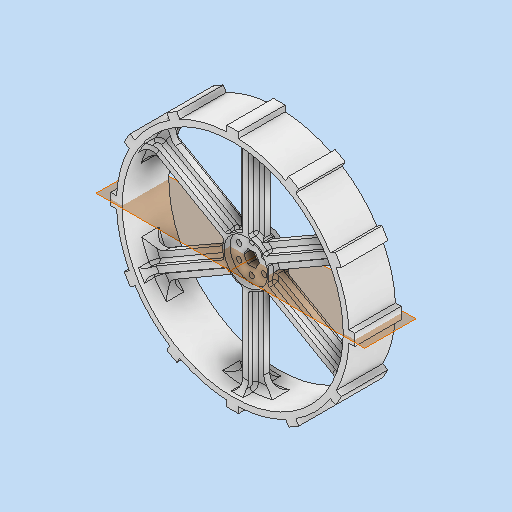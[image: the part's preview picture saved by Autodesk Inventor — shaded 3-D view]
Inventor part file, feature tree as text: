
AUTODESK INVENTOR PART (.ipt)
format: ipt  version: 2023 (Build 270158000, 158)  size: 903,168 bytes
history: native  units: in
note: dims shown in document units (in); Inventor stores cm internally (conversion verified against a paired STEP export)
features: fillet x5, sketch x5, extrude x4, pattern_circular x2
ambient origin geometry x8: Origin, YZ Plane, XZ Plane, XY Plane, X Axis, Y Axis, Z Axis, Center Point
bodies: Solid1 (feature_tree)
feature tree (16):
  extrude  "Extrusion1"  Depth=0.25in
  extrude  "Extrusion2"  Depth=2.0in
  extrude  "Extrusion3"  Depth=0.375in TaperAngle=0.0deg
  extrude  "Extrusion4"  Depth=0.25in
  fillet  "Fillet2"  Radius=0.875in
  fillet  "Fillet3"  Radius=0.25in
  fillet  "Fillet4"  Radius=0.875in
  fillet  "Fillet1"  Radius=0.9375in
  fillet  "Fillet5"  Radius=0.25in
  pattern_circular  "Circular Pattern1"  [2 undecoded]
  pattern_circular  "Circular Pattern5"  [2 undecoded]
  sketch  "Sketch1"  dims[d0=10.0in d2=0.25in]
  sketch  "Sketch2"  dims[d3=2.0in d4=0.0in d5=2.0in]
  sketch  "Sketch3"  dims[d6=0.5787in d7=0.375in d8=0.0in]
  sketch  "Sketch5"  dims[d9=2.0in d10=0.0625in d11=0.875in d12=0.0in d15=0.25in d16=0.875in d17=0.9375in d18=0.25in]
  sketch  "Sketch9"  dims[d20=0.875in d21=0.0in d22=0.125in d23=0.5in d24=0.375in d25=0.25in d26=0.125in d27=2.3622in d28=360.0deg d30=0.2362in d31=0.625in d32=2.3622in d34=360.0deg d56=0.0in d57=0.5in d58=2.0in d59=0.25in d60=0.0in d61=4.7244in d62=360.0deg]
note: 4 required parameter values undecoded (feature->parameter linkage not recoverable at this tier; creation-order binding heuristic only, values carry confidence <= 0.55)
